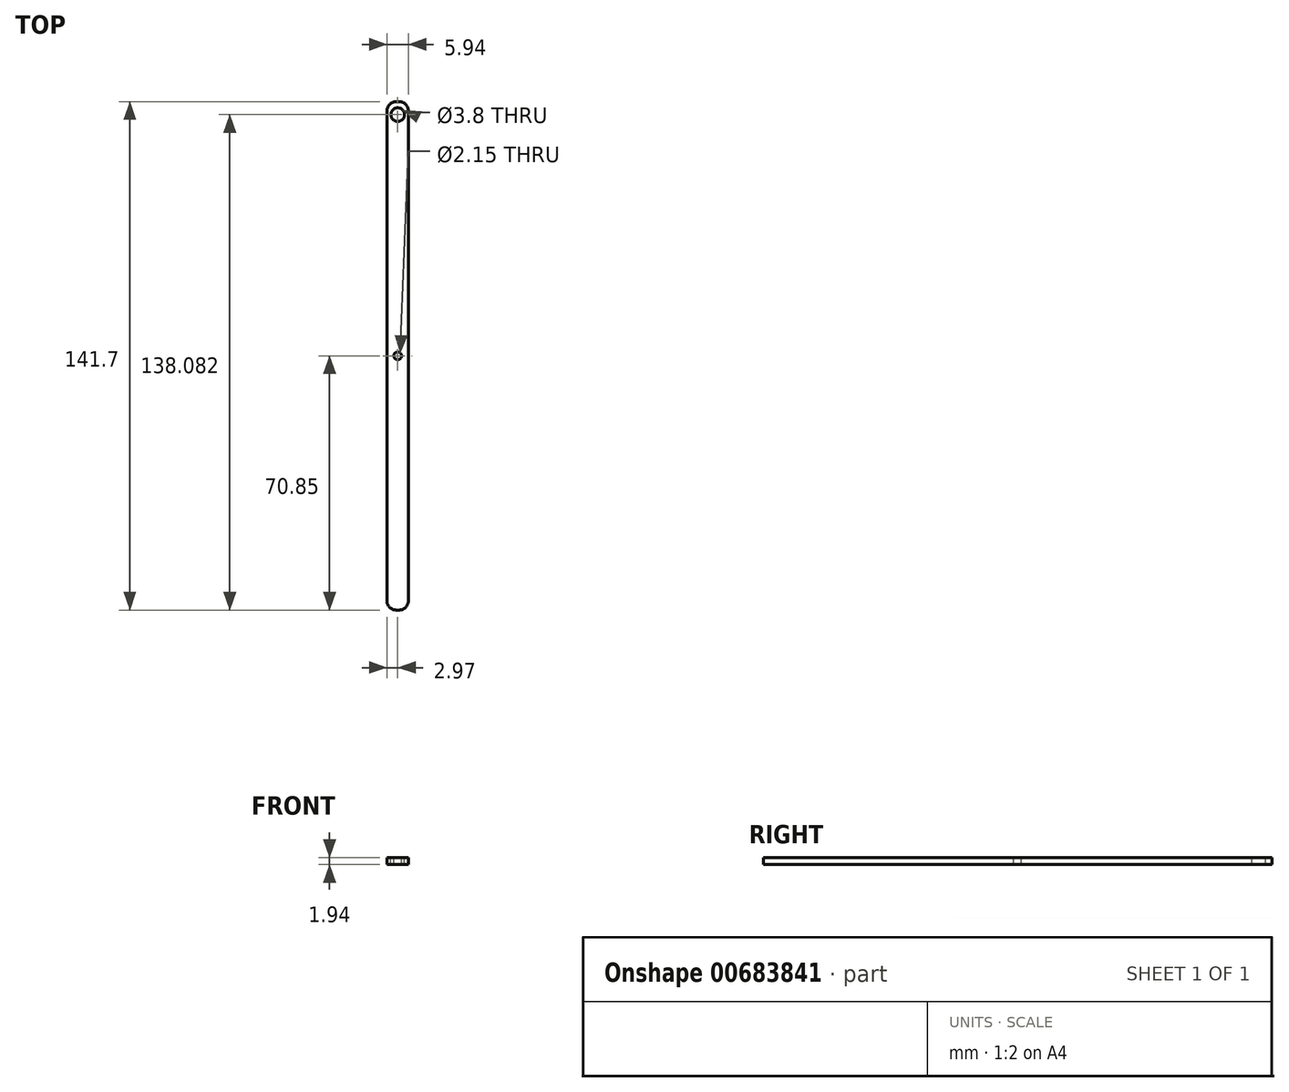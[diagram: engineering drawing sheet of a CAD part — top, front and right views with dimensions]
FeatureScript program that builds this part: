
annotation { "Feature Type Name" : "Feature", "Feature Type Description" : "" }
export const myFeature = defineFeature(function(context is Context, id is Id, definition is map)
    precondition{}
    {
        {
            var Q0;
            Q0=qCreatedBy(makeId("Front.planeOp"),FACE);
            var sketch = newSketch(context, id + "F0", { "sketchPlane" : qUnion([Q0])});
            skLineSegment(sketch, "E0.bottom", {"start": v(2.97, -0.97) * mm, "end": v(-2.97, -0.97) * mm});
            skLineSegment(sketch, "E0.top", {"start": v(2.97, 0.97) * mm, "end": v(-2.97, 0.97) * mm});
            skLineSegment(sketch, "E0.left", {"start": v(2.97, -0.97) * mm, "end": v(2.97, 0.97) * mm});
            skLineSegment(sketch, "E0.right", {"start": v(-2.97, -0.97) * mm, "end": v(-2.97, 0.97) * mm});
            skPoint(sketch, "E0.middle", {"position": v(0, 0) * mm});
            skSolve(sketch);
        }
        {
            var Q0;
            Q0=makeQuery(id+"F0.imprint","IMPRINT",FACE,{"disambiguationData":[TD([[makeQuery(id+"F0.imprint","IMPRINT",EDGE,{"derivedFrom":sQuery(id+"F0.wireOp",EDGE,"E0.bottom")}),-1.0]])]});
            extrude(context, id + "F1", {"entities" : qUnion([Q0]), "depth" : 70.85 * mm, "offsetDistance" : 25.4 * mm, "hasSecondDirection" : true, "secondDirectionOppositeDirection" : true, "secondDirectionDepth" : 70.85 * mm});
        }
        {
            var Q0;
            Q0=makeQuery(id+"F1.opExtrude","CAP_EDGE",EDGE,{"disambiguationData":[OSD([sQuery(id+"F0.wireOp",EDGE,"E0.left")])],"isStart":false});
            var Q1;
            Q1=makeQuery(id+"F1.opExtrude","CAP_EDGE",EDGE,{"disambiguationData":[OSD([sQuery(id+"F0.wireOp",EDGE,"E0.right")])],"isStart":false});
            var Q2;
            Q2=makeQuery(id+"F1.opExtrude","CAP_EDGE",EDGE,{"disambiguationData":[OSD([sQuery(id+"F0.wireOp",EDGE,"E0.left")])],"isStart":true});
            var Q3;
            Q3=makeQuery(id+"F1.opExtrude","CAP_EDGE",EDGE,{"disambiguationData":[OSD([sQuery(id+"F0.wireOp",EDGE,"E0.right")])],"isStart":true});
            fillet(context, id + "F2", {"entities" : qUnion([Q0, Q1, Q2, Q3]), "radius" : 2.54 * mm, "tangentPropagation" : true, "allowEdgeOverflow" : false});
        }
        {
            var Q0;
            Q0=makeQuery(id+"F1.opExtrude","SWEPT_FACE",FACE,{"disambiguationData":[OSD([sQuery(id+"F0.wireOp",EDGE,"E0.top")])]});
            var sketch = newSketch(context, id + "F3", { "sketchPlane" : qUnion([Q0])});
            skCircle(sketch, "E1", {"center": v(0, 67.23) * mm, "radius": 1.9 * mm});
            skSolve(sketch);
        }
        {
            var Q0;
            Q0=makeQuery(id+"F3.imprint","IMPRINT",FACE,{"disambiguationData":[TD([[makeQuery(id+"F3.imprint","IMPRINT",EDGE,{"derivedFrom":sQuery(id+"F3.wireOp",EDGE,"E1")}),1.0]])]});
            extrude(context, id + "F4", {"entities" : qUnion([Q0]), "operationType" : NewBodyOperationType.REMOVE, "oppositeDirection" : true, "depth" : 2.36 * mm, "offsetDistance" : 25.4 * mm});
        }
        {
            var Q0;
            Q0=makeQuery(id+"F1.opExtrude","SWEPT_FACE",FACE,{"disambiguationData":[OSD([sQuery(id+"F0.wireOp",EDGE,"E0.top")])]});
            var sketch = newSketch(context, id + "F5", { "sketchPlane" : qUnion([Q0])});
            skCircle(sketch, "E2", {"center": v(0, 0) * mm, "radius": 1.08 * mm});
            skSolve(sketch);
        }
        {
            var Q0;
            Q0 = qSketchRegion(id + "F5", true);
            extrude(context, id + "F6", {"entities" : qUnion([Q0]), "operationType" : NewBodyOperationType.REMOVE, "oppositeDirection" : true, "depth" : 2.02 * mm, "offsetDistance" : 25.4 * mm});
        }
    });
